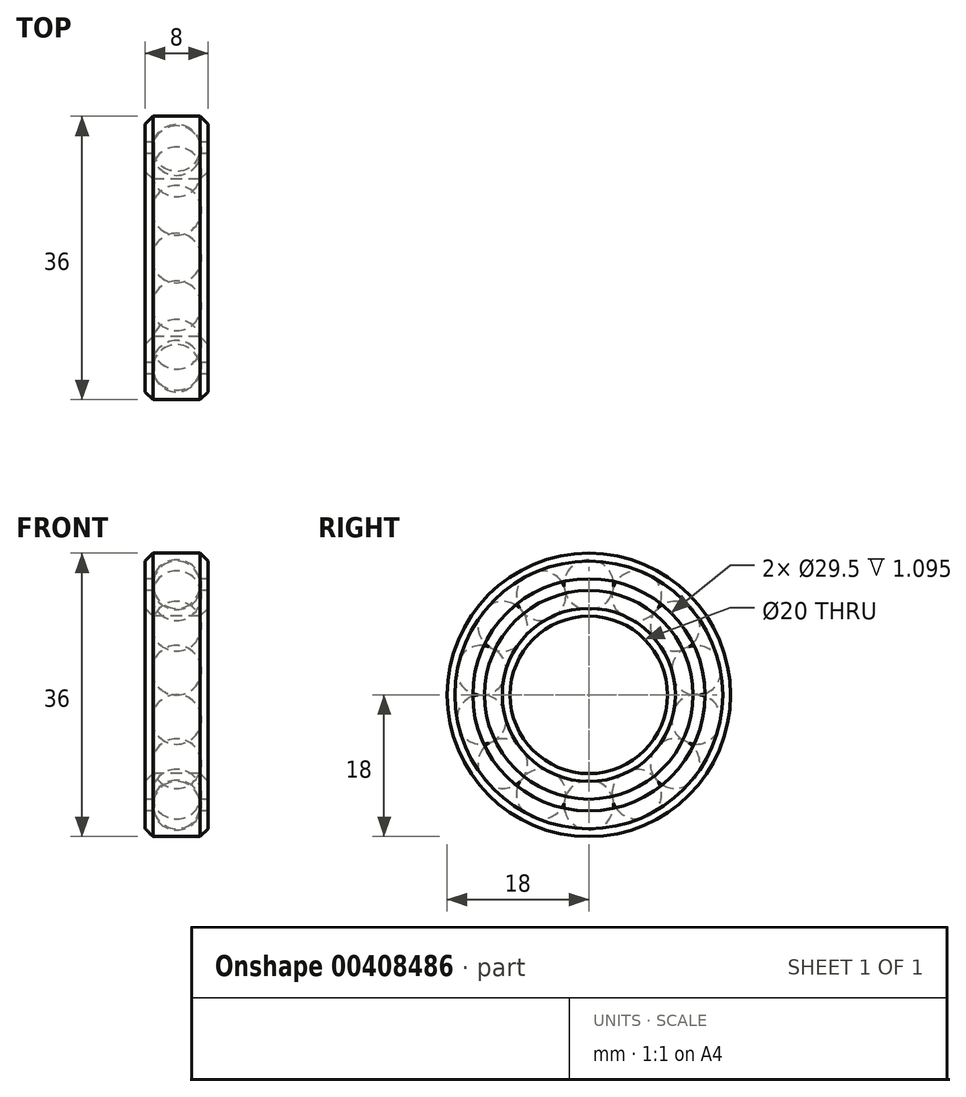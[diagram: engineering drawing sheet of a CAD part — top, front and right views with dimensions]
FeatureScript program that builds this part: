
annotation { "Feature Type Name" : "Feature", "Feature Type Description" : "" }
export const myFeature = defineFeature(function(context is Context, id is Id, definition is map)
    precondition{}
    {
        {
            var Q0;
            Q0=qCreatedBy(makeId("Front.planeOp"),FACE);
            var sketch = newSketch(context, id + "F0", { "sketchPlane" : qUnion([Q0])});
            skLineSegment(sketch, "E0", {"start": v(-4, 14) * mm, "end": v(4, 14) * mm, "construction": true});
            skLineSegment(sketch, "E1", {"start": v(-11.33, 0) * mm, "end": v(11.52, 0) * mm, "construction": true});
            skLineSegment(sketch, "E2", {"start": v(2.9, 14.75) * mm, "end": v(4, 14.75) * mm});
            skLineSegment(sketch, "E3", {"start": v(4, 14.75) * mm, "end": v(4, 18) * mm});
            skLineSegment(sketch, "E4", {"start": v(4, 18) * mm, "end": v(-4, 18) * mm});
            skLineSegment(sketch, "E5", {"start": v(-4, 18) * mm, "end": v(-4, 14.75) * mm});
            skLineSegment(sketch, "E6", {"start": v(-4, 14.75) * mm, "end": v(-2.9, 14.75) * mm});
            skArc(sketch, "E7", {"start": v(2.9, 14.75) * mm, "mid": v(0, 17) * mm, "end": v(-2.9, 14.75) * mm});
            skLineSegment(sketch, "E8.MirrorCS", {"start": v(-4, 13.25) * mm, "end": v(-2.9, 13.25) * mm});
            skArc(sketch, "E9.MirrorCS", {"start": v(2.9, 13.25) * mm, "mid": v(0, 11) * mm, "end": v(-2.9, 13.25) * mm});
            skLineSegment(sketch, "E10.MirrorCS", {"start": v(-4, 10) * mm, "end": v(-4, 13.25) * mm});
            skLineSegment(sketch, "E11.MirrorCS", {"start": v(2.9, 13.25) * mm, "end": v(4, 13.25) * mm});
            skLineSegment(sketch, "E12.MirrorCS", {"start": v(4, 10) * mm, "end": v(-4, 10) * mm});
            skLineSegment(sketch, "E13.MirrorCS", {"start": v(4, 13.25) * mm, "end": v(4, 10) * mm});
            skSolve(sketch);
        }
        {
            var Q0;
            Q0=makeQuery(id+"F0.imprint","IMPRINT",FACE,{"disambiguationData":[TD([[makeQuery(id+"F0.imprint","IMPRINT",EDGE,{"derivedFrom":sQuery(id+"F0.wireOp",EDGE,"E2")}),1.0]])]});
            var Q1;
            Q1=makeQuery(id+"F0.imprint","IMPRINT",FACE,{"disambiguationData":[TD([[makeQuery(id+"F0.imprint","IMPRINT",EDGE,{"derivedFrom":sQuery(id+"F0.wireOp",EDGE,"E8.MirrorCS")}),-1.0]])]});
            var Q2;
            Q2=sQuery(id+"F0.wireOp",EDGE,"E1");
            revolve(context, id + "F1", {"entities" : qUnion([Q0, Q1]), "axis" : qUnion([Q2]), "revolveType" : RevolveType.FULL});
        }
        {
            var Q0;
            Q0=makeQuery(id+"F1.opRevolve","SWEPT_EDGE",EDGE,{"disambiguationData":[OSD([sQuery(id+"F0.wireOp",EDGE,"E3"),sQuery(id+"F0.wireOp",EDGE,"E4")])]});
            var Q1;
            Q1=makeQuery(id+"F1.opRevolve","SWEPT_EDGE",EDGE,{"disambiguationData":[OSD([sQuery(id+"F0.wireOp",EDGE,"E12.MirrorCS"),sQuery(id+"F0.wireOp",EDGE,"E13.MirrorCS")])]});
            var Q2;
            Q2=makeQuery(id+"F1.opRevolve","SWEPT_EDGE",EDGE,{"disambiguationData":[OSD([sQuery(id+"F0.wireOp",EDGE,"E10.MirrorCS"),sQuery(id+"F0.wireOp",EDGE,"E12.MirrorCS")])]});
            var Q3;
            Q3=makeQuery(id+"F1.opRevolve","SWEPT_EDGE",EDGE,{"disambiguationData":[OSD([sQuery(id+"F0.wireOp",EDGE,"E4"),sQuery(id+"F0.wireOp",EDGE,"E5")])]});
            chamfer(context, id + "F2", {"entities" : qUnion([Q0, Q1, Q2, Q3]), "chamferType" : ChamferType.OFFSET_ANGLE, "width" : 1 * mm, "oppositeDirection" : false, "angle" : 45 * degree, "tangentPropagation" : true});
        }
        {
            var Q0;
            Q0=qCreatedBy(makeId("Front.planeOp"),FACE);
            var sketch = newSketch(context, id + "F3", { "sketchPlane" : qUnion([Q0])});
            skLineSegment(sketch, "E14.0", {"start": v(-4, 14) * mm, "end": v(4, 14) * mm});
            skArc(sketch, "E15", {"start": v(3.15, 14) * mm, "mid": v(0, 17.15) * mm, "end": v(-3.15, 14) * mm});
            skSolve(sketch);
        }
        {
            var Q0;
            {var subQ0=sQuery(id+"F3.wireOp",EDGE,"E15");Q0=makeQuery(id+"F3.imprint","IMPRINT",FACE,{"disambiguationData":[TD([[makeQuery(id+"F3.imprint","IMPRINT",EDGE,{"derivedFrom":subQ0}),1.0]])]});}
            var Q1;
            Q1=sQuery(id+"F0.wireOp",EDGE,"E0");
            revolve(context, id + "F4", {"entities" : qUnion([Q0]), "axis" : qUnion([Q1]), "revolveType" : RevolveType.FULL});
        }
        {
            var Q0;
            Q0=makeQuery(id+"F4.opRevolve","SWEPT_BODY",BODY,{"disambiguationData":[OSD([sQuery(id+"F3.wireOp",EDGE,"E14.0"),sQuery(id+"F3.wireOp",EDGE,"E15")])]});
            var Q1;
            {var subQ0=sQuery(id+"F0.wireOp",EDGE,"E13.MirrorCS");Q1=makeQuery(id+"F2.opChamfer","BLEND_EDGE",EDGE,{"blendedFrom":[makeQuery(id+"F1.opRevolve","SWEPT_EDGE",EDGE,{"disambiguationData":[OSD([sQuery(id+"F0.wireOp",EDGE,"E12.MirrorCS"),subQ0])]}),makeQuery(id+"F1.opRevolve","SWEPT_FACE",FACE,{"disambiguationData":[OSD([subQ0])]})],"blendedInto":[makeQuery(id+"F1.opRevolve","SWEPT_FACE",FACE,{"disambiguationData":[OSD([subQ0])]})]});}
            circularPattern(context, id + "F5", {"entities" : qUnion([Q0]), "axis" : qUnion([Q1]), "angle" : 360 * degree, "instanceCount" : 14, "equalSpace" : true});
        }
    });
